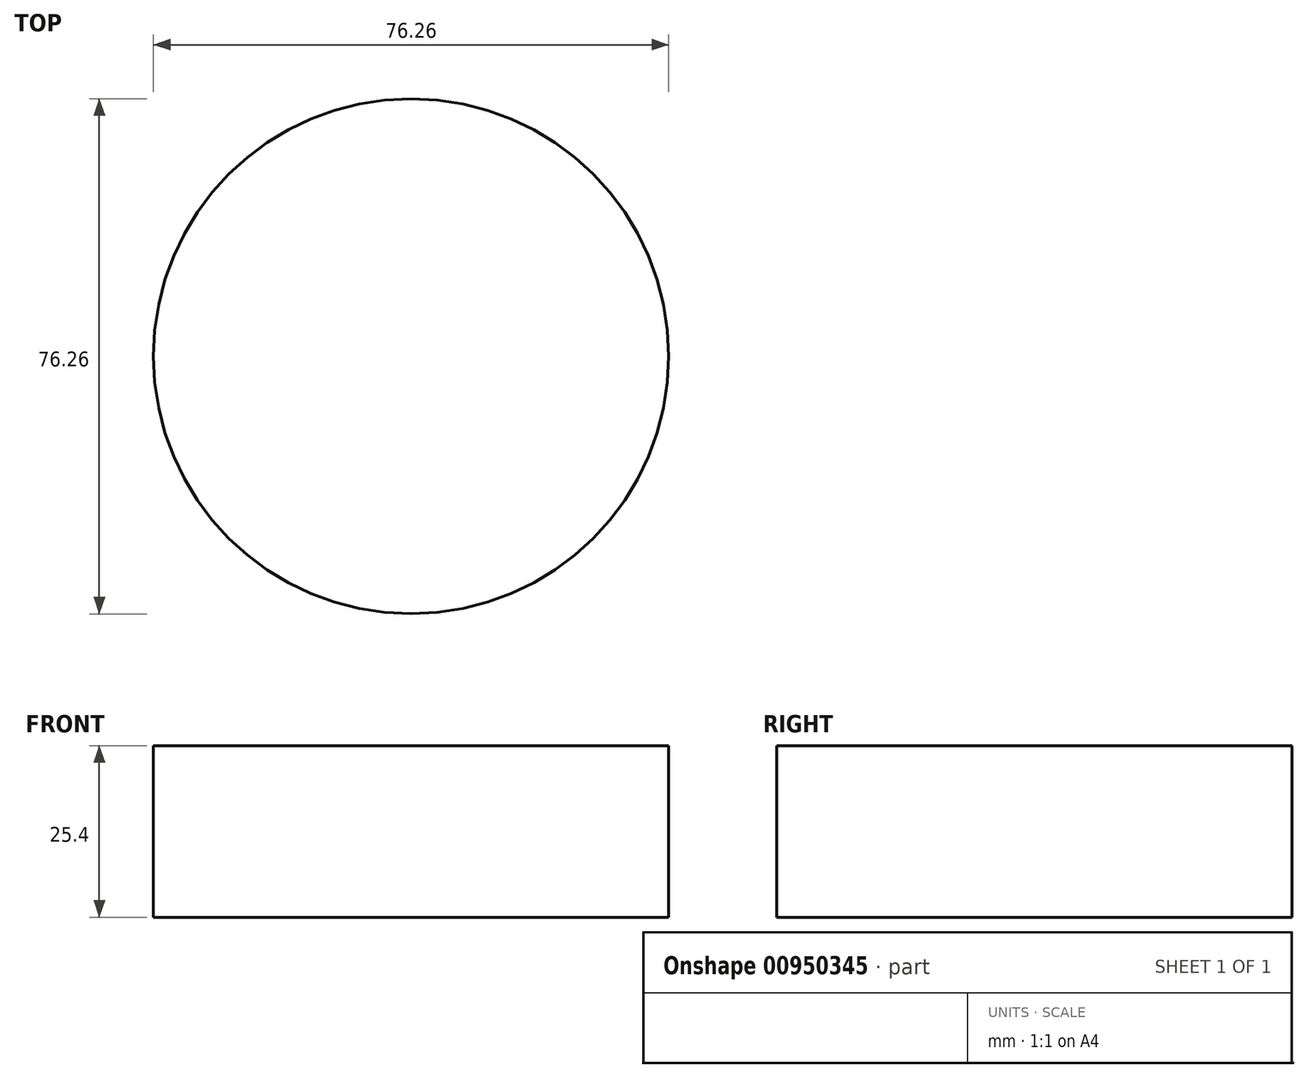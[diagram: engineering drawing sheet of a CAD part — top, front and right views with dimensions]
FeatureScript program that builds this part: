
annotation { "Feature Type Name" : "Feature", "Feature Type Description" : "" }
export const myFeature = defineFeature(function(context is Context, id is Id, definition is map)
    precondition{}
    {
        {
            var Q0;
            Q0=qCreatedBy(makeId("Top.planeOp"),FACE);
            var sketch = newSketch(context, id + "F0", { "sketchPlane" : qUnion([Q0])});
            skCircle(sketch, "E0", {"center": v(0, 0) * mm, "radius": 38.13 * mm});
            skSolve(sketch);
        }
        {
            var Q0;
            Q0=makeQuery(id+"F0.imprint","IMPRINT",FACE,{"disambiguationData":[TD([[makeQuery(id+"F0.imprint","IMPRINT",EDGE,{"derivedFrom":sQuery(id+"F0.wireOp",EDGE,"E0")}),1.0]])]});
            extrude(context, id + "F1", {"entities" : qUnion([Q0]), "depth" : 25.4 * mm, "offsetDistance" : 25.4 * mm});
        }
    });
